FCSTD DOCUMENT  (FreeCAD 0.20R29410 (Git))
Label: PinzaDemoMemoria
License: All rights reserved
LicenseURL: http://en.wikipedia.org/wiki/All_rights_reserved
objects: Sketcher::SketchObject×1, PartDesign::Body×1
note: 2 computed .brp shape members not serialized (recipe doc carries the construction recipe); baked Part::Feature solids carry a one-line shape summary decoded from their .brp

FEATURE [Sketcher::SketchObject] Sketch
  FullyConstrained = false
  MapMode = 5
  Support = -> [XY_Plane]
  sketch-geometry (15):
    g0: LineSegment StartX=-15.2888 StartY=38.2733 StartZ=0 EndX=-15.2888 EndY=23.2733 EndZ=0
    g1: LineSegment StartX=-15.2888 StartY=23.2733 StartZ=0 EndX=-25.8954 EndY=12.6667 EndZ=0
    g2: LineSegment StartX=-13.1066 StartY=0 StartZ=0 EndX=-2.5 EndY=10.6066 EndZ=0
    g3: LineSegment StartX=-2.5 StartY=10.6066 StartZ=0 EndX=2.5 EndY=10.6066 EndZ=0
    g4: LineSegment StartX=2.5 StartY=10.6066 StartZ=0 EndX=13.1066 EndY=0 EndZ=0
    g5: LineSegment StartX=-15.2888 StartY=23.2733 StartZ=0 EndX=-2.5 EndY=10.6066 EndZ=0
    g6: LineSegment StartX=-25.8954 StartY=12.6667 StartZ=0 EndX=-13.1066 EndY=0 EndZ=0
    g7: LineSegment StartX=-25.8954 StartY=12.6667 StartZ=0 EndX=-15.2888 EndY=38.2733 EndZ=0
    g8: LineSegment StartX=15.2888 StartY=38.2733 StartZ=0 EndX=15.2888 EndY=23.2733 EndZ=0
    g9: LineSegment StartX=15.2888 StartY=23.2733 StartZ=0 EndX=25.8954 EndY=12.6667 EndZ=0
    g10: LineSegment StartX=15.2888 StartY=38.2733 StartZ=0 EndX=25.8954 EndY=12.6667 EndZ=0
    g11: LineSegment StartX=15.2888 StartY=23.2733 StartZ=0 EndX=2.5 EndY=10.6066 EndZ=0
    g12: LineSegment StartX=25.8954 StartY=12.6667 StartZ=0 EndX=13.1066 EndY=0 EndZ=0
    g13: LineSegment StartX=-25.8954 StartY=12.6667 StartZ=0 EndX=0 EndY=10.3371 EndZ=0
    g14: LineSegment StartX=0 StartY=10.3371 StartZ=0 EndX=25.8954 EndY=12.6667 EndZ=0
  constraints (38):
    c: Vertical(g0)
    c: Coincident(g1,g0)
    c: Angle(g0,g1) = 2.35619
    c: DistanceY(g0,g0) = 15
    c: Distance(g1) = 15
    c: Coincident(g3,g2)
    c: Coincident(g4,g3)
    c: Coincident(g5,g0)
    c: Coincident(g5,g2)
    c: Coincident(g6,g1)
    c: Coincident(g6,g2)
    c: Distance(g2) = 15
    c: Distance(g4) = 15
    c: Distance(g5) = 18
    c: Distance(g6) = 18
    c: Symmetric(g4,g2,g-1)
    c: Coincident(g7,g1)
    c: Coincident(g7,g0)
    c: Vertical(g8)
    c: Coincident(g9,g8)
    c: Coincident(g10,g8)
    c: Coincident(g10,g9)
    c: Coincident(g11,g8)
    c: Coincident(g11,g3)
    c: Coincident(g12,g9)
    c: Coincident(g12,g4)
    c: Distance(g9) = 15
    c: Distance(g11) = 18
    c: Distance(g12) = 18
    c: Distance(g8) = 15
    c: Coincident(g13,g1)
    c: PointOnObject(g13,g-2)
    c: Coincident(g14,g13)
    c: Coincident(g14,g9)
    c: Distance(g14) = 26
    c: Equal(g14,g13)
    c: Distance(g3) = 5
    c: Symmetric(g3,g2,g-2)
FEATURE [PartDesign::Body] Body
  Group = -> [Sketch]
  Origin = -> Origin
